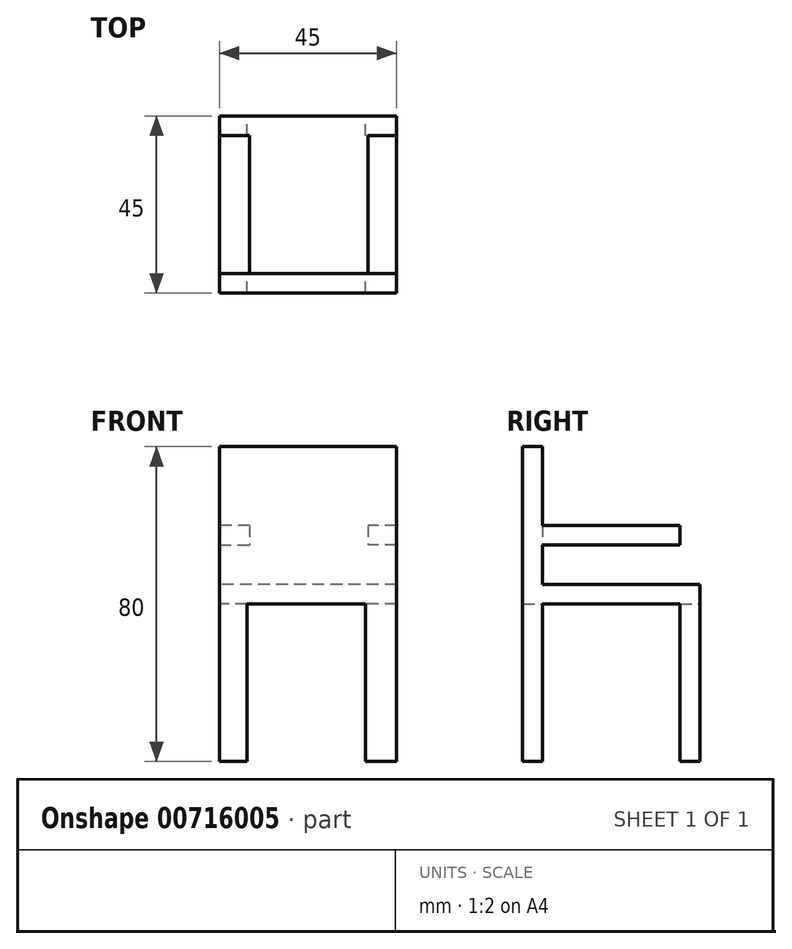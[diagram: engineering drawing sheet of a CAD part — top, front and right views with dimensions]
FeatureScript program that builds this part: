
annotation { "Feature Type Name" : "Feature", "Feature Type Description" : "" }
export const myFeature = defineFeature(function(context is Context, id is Id, definition is map)
    precondition{}
    {
        {
            var Q0;
            Q0=qCreatedBy(makeId("Right.planeOp"),FACE);
            var sketch = newSketch(context, id + "F0", { "sketchPlane" : qUnion([Q0])});
            skLineSegment(sketch, "E0", {"start": v(-26.38, 25) * mm, "end": v(-26.38, -55) * mm});
            skLineSegment(sketch, "E1", {"start": v(-26.38, -55) * mm, "end": v(-21.38, -55) * mm});
            skLineSegment(sketch, "E2", {"start": v(-21.38, -55) * mm, "end": v(-21.38, -15) * mm});
            skLineSegment(sketch, "E3", {"start": v(-21.38, -15) * mm, "end": v(13.62, -15) * mm});
            skLineSegment(sketch, "E4", {"start": v(13.62, -15) * mm, "end": v(13.62, -55) * mm});
            skLineSegment(sketch, "E5", {"start": v(13.62, -55) * mm, "end": v(18.62, -55) * mm});
            skLineSegment(sketch, "E6", {"start": v(18.62, -55) * mm, "end": v(18.62, -10) * mm});
            skLineSegment(sketch, "E7", {"start": v(18.62, -10) * mm, "end": v(-21.38, -10) * mm});
            skLineSegment(sketch, "E8", {"start": v(-21.38, -10) * mm, "end": v(-21.38, 0) * mm});
            skLineSegment(sketch, "E9", {"start": v(-21.38, 0) * mm, "end": v(13.62, 0) * mm});
            skLineSegment(sketch, "E10", {"start": v(13.62, 0) * mm, "end": v(13.62, 5) * mm});
            skLineSegment(sketch, "E11", {"start": v(13.62, 5) * mm, "end": v(-21.38, 5) * mm});
            skLineSegment(sketch, "E12", {"start": v(-21.38, 5) * mm, "end": v(-21.38, 25) * mm});
            skLineSegment(sketch, "E13", {"start": v(-21.38, 25) * mm, "end": v(-26.38, 25) * mm});
            skSolve(sketch);
        }
        {
            var Q0;
            Q0=makeQuery(id+"F0.imprint","IMPRINT",FACE,{"disambiguationData":[TD([[makeQuery(id+"F0.imprint","IMPRINT",EDGE,{"derivedFrom":sQuery(id+"F0.wireOp",EDGE,"E0")}),1.0]])]});
            extrude(context, id + "F1", {"entities" : qUnion([Q0]), "depth" : 45 * mm, "offsetDistance" : 25 * mm});
        }
        {
            var Q0;
            Q0=qCreatedBy(makeId("Front.planeOp"),FACE);
            var sketch = newSketch(context, id + "F2", { "sketchPlane" : qUnion([Q0])});
            skLineSegment(sketch, "E14.bottom", {"start": v(37.04, -15) * mm, "end": v(7.04, -15) * mm});
            skLineSegment(sketch, "E14.top", {"start": v(37.04, -55) * mm, "end": v(7.04, -55) * mm});
            skLineSegment(sketch, "E14.left", {"start": v(37.04, -15) * mm, "end": v(37.04, -55) * mm});
            skLineSegment(sketch, "E14.right", {"start": v(7.04, -15) * mm, "end": v(7.04, -55) * mm});
            skSolve(sketch);
        }
        {
            var Q0;
            Q0 = qSketchRegion(id + "F2", true);
            extrude(context, id + "F3", {"entities" : qUnion([Q0]), "operationType" : NewBodyOperationType.REMOVE, "endBound" : BoundingType.THROUGH_ALL, "depth" : 0.4 * mm, "offsetDistance" : 25 * mm, "hasSecondDirection" : true, "secondDirectionOppositeDirection" : true, "secondDirectionDepth" : 25 * mm});
        }
        {
            var Q0;
            Q0=qCreatedBy(makeId("Front.planeOp"),FACE);
            var sketch = newSketch(context, id + "F4", { "sketchPlane" : qUnion([Q0])});
            skLineSegment(sketch, "E15.bottom", {"start": v(37.68, 5) * mm, "end": v(7.68, 5) * mm});
            skLineSegment(sketch, "E15.top", {"start": v(37.68, 0) * mm, "end": v(7.68, 0) * mm});
            skLineSegment(sketch, "E15.left", {"start": v(37.68, 5) * mm, "end": v(37.68, 0) * mm});
            skLineSegment(sketch, "E15.right", {"start": v(7.68, 5) * mm, "end": v(7.68, 0) * mm});
            skSolve(sketch);
        }
        {
            var Q0;
            Q0 = qSketchRegion(id + "F4", true);
            extrude(context, id + "F5", {"entities" : qUnion([Q0]), "operationType" : NewBodyOperationType.REMOVE, "endBound" : BoundingType.THROUGH_ALL, "oppositeDirection" : true, "depth" : 26.8 * mm, "offsetDistance" : 25 * mm, "hasSecondDirection" : true, "secondDirectionOppositeDirection" : false, "secondDirectionDepth" : 21.38 * mm});
        }
    });
